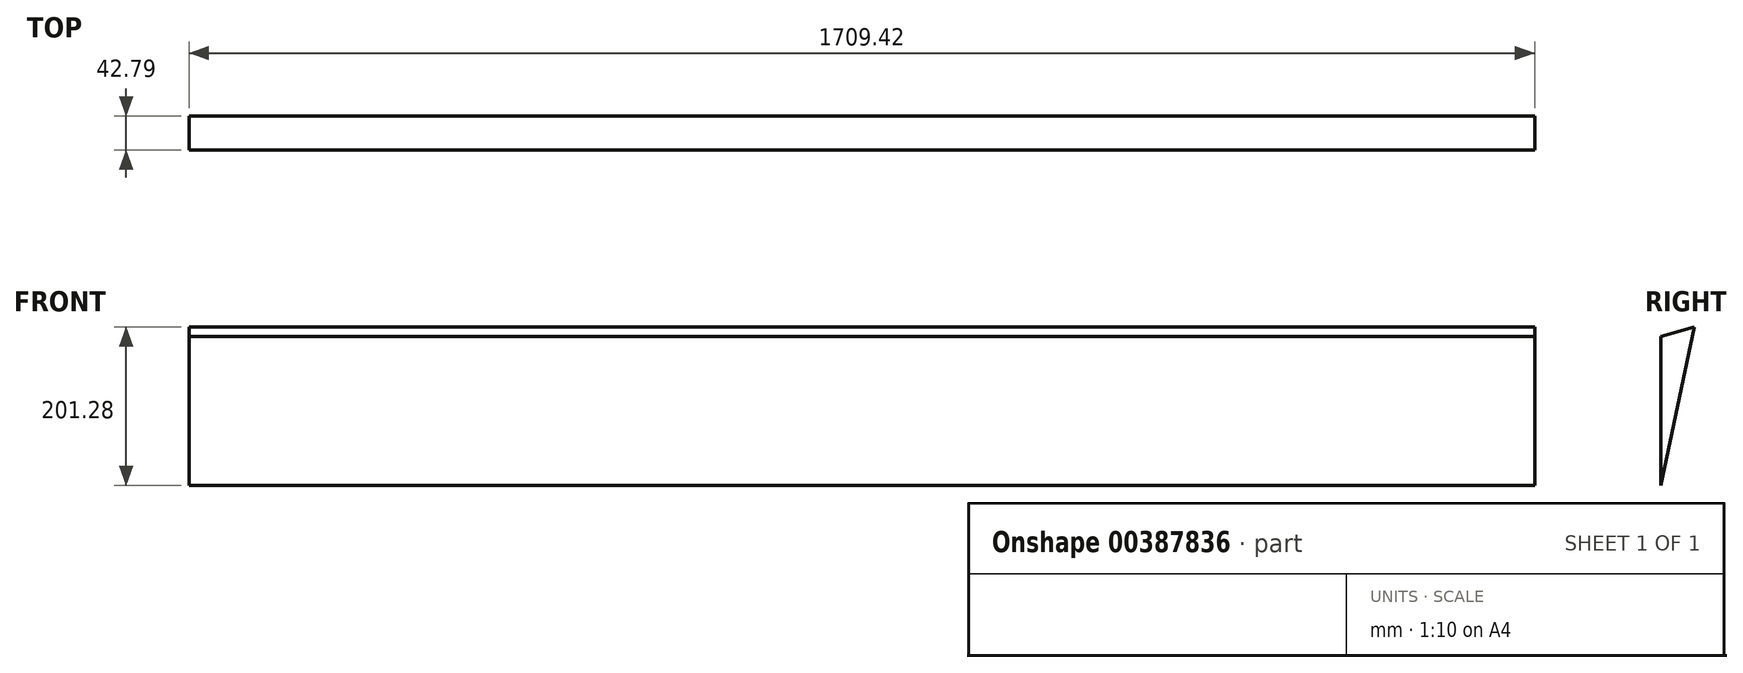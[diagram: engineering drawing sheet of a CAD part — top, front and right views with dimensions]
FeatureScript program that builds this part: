
annotation { "Feature Type Name" : "Feature", "Feature Type Description" : "" }
export const myFeature = defineFeature(function(context is Context, id is Id, definition is map)
    precondition{}
    {
        {
            var Q0;
            Q0=qCreatedBy(makeId("Right.planeOp"),FACE);
            var sketch = newSketch(context, id + "F0", { "sketchPlane" : qUnion([Q0])});
            skLineSegment(sketch, "E0", {"start": v(-41.7, 83.38) * mm, "end": v(-41.7, -105.85) * mm});
            skLineSegment(sketch, "E1", {"start": v(-41.7, -105.85) * mm, "end": v(1.09, 95.43) * mm});
            skLineSegment(sketch, "E2", {"start": v(1.09, 95.43) * mm, "end": v(-41.7, 83.38) * mm});
            skSolve(sketch);
        }
        {
            var Q0;
            Q0 = qSketchRegion(id + "F0", true);
            extrude(context, id + "F1", {"entities" : qUnion([Q0]), "depth" : 1709.42 * mm});
        }
    });
